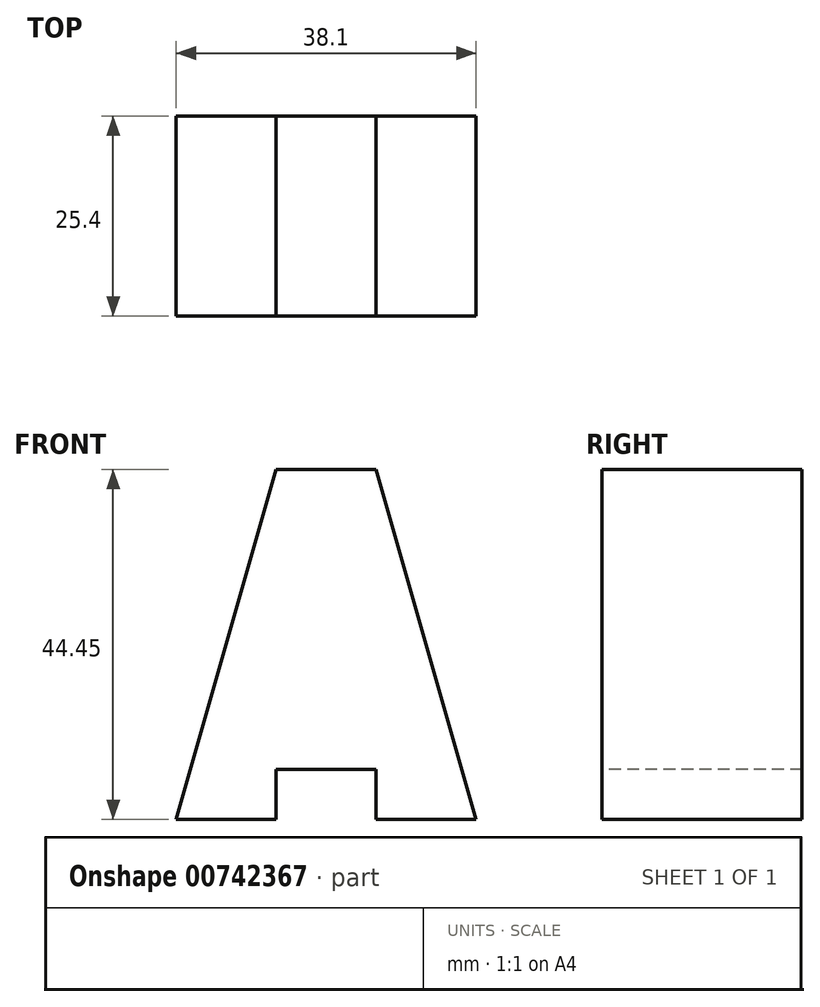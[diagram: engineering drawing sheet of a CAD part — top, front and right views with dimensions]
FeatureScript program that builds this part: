
annotation { "Feature Type Name" : "Feature", "Feature Type Description" : "" }
export const myFeature = defineFeature(function(context is Context, id is Id, definition is map)
    precondition{}
    {
        {
            var Q0;
            Q0=qCreatedBy(makeId("Front.planeOp"),FACE);
            var sketch = newSketch(context, id + "F0", { "sketchPlane" : qUnion([Q0])});
            skLineSegment(sketch, "E0", {"start": v(0, 44.45) * mm, "end": v(0, 0) * mm});
            skLineSegment(sketch, "E1", {"start": v(0, 0) * mm, "end": v(-38.1, 0) * mm});
            skLineSegment(sketch, "E2", {"start": v(-38.1, 0) * mm, "end": v(-38.1, 44.45) * mm});
            skLineSegment(sketch, "E3", {"start": v(-38.1, 44.45) * mm, "end": v(0, 44.45) * mm});
            skSolve(sketch);
        }
        {
            var Q0;
            Q0 = qSketchRegion(id + "F0", true);
            extrude(context, id + "F1", {"entities" : qUnion([Q0]), "depth" : 25.4 * mm, "offsetDistance" : 25.4 * mm});
        }
        {
            var Q0;
            Q0=makeQuery(id+"F1.opExtrude","CAP_FACE",FACE,{"disambiguationData":[OSD([sQuery(id+"F0.wireOp",EDGE,"E0"),sQuery(id+"F0.wireOp",EDGE,"E1"),sQuery(id+"F0.wireOp",EDGE,"E2"),sQuery(id+"F0.wireOp",EDGE,"E3")])],"isStart":false});
            var sketch = newSketch(context, id + "F2", { "sketchPlane" : qUnion([Q0])});
            skLineSegment(sketch, "E4", {"start": v(-12.7, 44.45) * mm, "end": v(0, 0) * mm});
            skLineSegment(sketch, "E5", {"start": v(0, 0) * mm, "end": v(-38.1, 0) * mm});
            skLineSegment(sketch, "E6", {"start": v(-38.1, 0) * mm, "end": v(-25.4, 44.45) * mm});
            skLineSegment(sketch, "E7", {"start": v(-25.4, 44.45) * mm, "end": v(-12.7, 44.45) * mm});
            skLineSegment(sketch, "E8", {"start": v(-38.1, 0) * mm, "end": v(0, 0) * mm});
            skSolve(sketch);
        }
        {
            var Q0;
            {var subQ0=sQuery(id+"F2.wireOp",EDGE,"E6");Q0=makeQuery(id+"F2.imprint","IMPRINT",FACE,{"disambiguationData":[TD([[makeQuery(id+"F2.imprint","IMPRINT",EDGE,{"derivedFrom":subQ0}),1.0]])]});}
            extrude(context, id + "F3", {"entities" : qUnion([Q0]), "operationType" : NewBodyOperationType.REMOVE, "endBound" : BoundingType.THROUGH_ALL, "oppositeDirection" : true, "depth" : 25.4 * mm, "offsetDistance" : 25.4 * mm});
        }
        {
            var Q0;
            Q0=makeQuery(id+"F1.opExtrude","CAP_FACE",FACE,{"disambiguationData":[OSD([sQuery(id+"F0.wireOp",EDGE,"E0"),sQuery(id+"F0.wireOp",EDGE,"E1"),sQuery(id+"F0.wireOp",EDGE,"E2"),sQuery(id+"F0.wireOp",EDGE,"E3")])],"isStart":false});
            var sketch = newSketch(context, id + "F4", { "sketchPlane" : qUnion([Q0])});
            skLineSegment(sketch, "E9", {"start": v(-12.7, 44.45) * mm, "end": v(0, 0) * mm});
            skSolve(sketch);
        }
        {
            var Q0;
            {var subQ0=sQuery(id+"F4.wireOp",EDGE,"E9");Q0=makeQuery(id+"F4.imprint","IMPRINT",FACE,{"disambiguationData":[TD([[makeQuery(id+"F4.imprint","IMPRINT",EDGE,{"derivedFrom":subQ0}),1.0]])]});}
            extrude(context, id + "F5", {"entities" : qUnion([Q0]), "operationType" : NewBodyOperationType.REMOVE, "endBound" : BoundingType.THROUGH_ALL, "oppositeDirection" : true, "depth" : 25.4 * mm, "offsetDistance" : 25.4 * mm});
        }
        {
            var Q0;
            Q0=makeQuery(id+"F1.opExtrude","CAP_FACE",FACE,{"disambiguationData":[OSD([sQuery(id+"F0.wireOp",EDGE,"E0"),sQuery(id+"F0.wireOp",EDGE,"E1"),sQuery(id+"F0.wireOp",EDGE,"E2"),sQuery(id+"F0.wireOp",EDGE,"E3")])],"isStart":false});
            var sketch = newSketch(context, id + "F6", { "sketchPlane" : qUnion([Q0])});
            skLineSegment(sketch, "E10", {"start": v(-25.4, 0) * mm, "end": v(-25.4, 6.35) * mm});
            skLineSegment(sketch, "E11", {"start": v(-25.4, 6.35) * mm, "end": v(-12.7, 6.35) * mm});
            skLineSegment(sketch, "E12", {"start": v(-12.7, 6.35) * mm, "end": v(-12.7, 0) * mm});
            skSolve(sketch);
        }
        {
            var Q0;
            {var subQ0=sQuery(id+"F6.wireOp",EDGE,"E10");Q0=makeQuery(id+"F6.imprint","IMPRINT",FACE,{"disambiguationData":[TD([[makeQuery(id+"F6.imprint","IMPRINT",EDGE,{"derivedFrom":subQ0}),-1.0]])]});}
            extrude(context, id + "F7", {"entities" : qUnion([Q0]), "operationType" : NewBodyOperationType.REMOVE, "endBound" : BoundingType.THROUGH_ALL, "oppositeDirection" : true, "depth" : 25.4 * mm, "offsetDistance" : 25.4 * mm});
        }
    });
